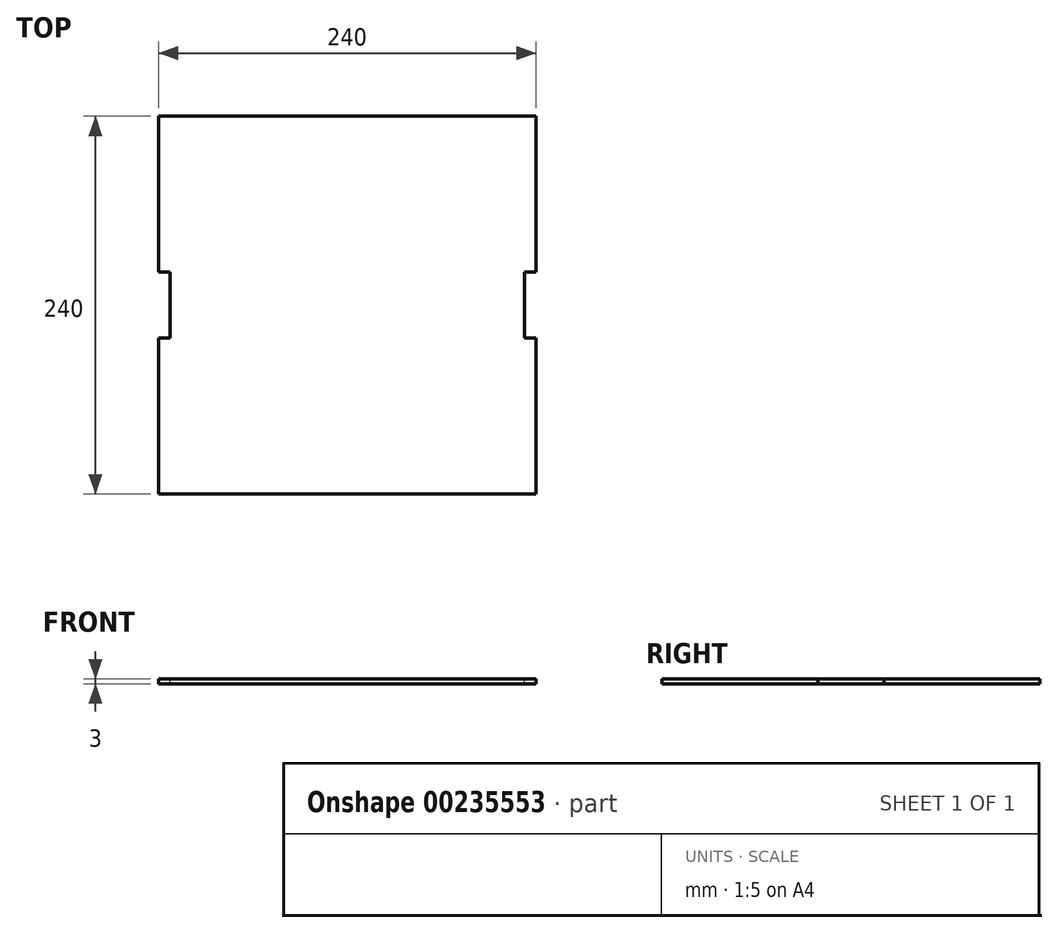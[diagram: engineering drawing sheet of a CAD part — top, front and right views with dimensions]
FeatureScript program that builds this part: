
annotation { "Feature Type Name" : "Feature", "Feature Type Description" : "" }
export const myFeature = defineFeature(function(context is Context, id is Id, definition is map)
    precondition{}
    {
        {
            var Q0;
            Q0=qCreatedBy(makeId("Top.planeOp"),FACE);
            var sketch = newSketch(context, id + "F0", { "sketchPlane" : qUnion([Q0])});
            skLineSegment(sketch, "E0.bottom", {"start": v(120, -120) * mm, "end": v(-120, -120) * mm});
            skLineSegment(sketch, "E0.top", {"start": v(120, 120) * mm, "end": v(-120, 120) * mm});
            skLineSegment(sketch, "E0.left", {"start": v(120, -120) * mm, "end": v(120, 120) * mm});
            skLineSegment(sketch, "E0.right", {"start": v(-120, -120) * mm, "end": v(-120, 120) * mm});
            skPoint(sketch, "E0.middle", {"position": v(0, 0) * mm});
            skSolve(sketch);
        }
        {
            var Q0;
            Q0=makeQuery(id+"F0.imprint","IMPRINT",FACE,{"disambiguationData":[TD([[makeQuery(id+"F0.imprint","IMPRINT",EDGE,{"derivedFrom":sQuery(id+"F0.wireOp",EDGE,"E0.bottom")}),-1.0]])]});
            extrude(context, id + "F1", {"entities" : qUnion([Q0]), "depth" : 3 * mm});
        }
        {
            var Q0;
            Q0=makeQuery(id+"F1.opExtrude","CAP_FACE",FACE,{"disambiguationData":[OSD([sQuery(id+"F0.wireOp",EDGE,"E0.bottom"),sQuery(id+"F0.wireOp",EDGE,"E0.top"),sQuery(id+"F0.wireOp",EDGE,"E0.left"),sQuery(id+"F0.wireOp",EDGE,"E0.right")])],"isStart":false});
            var sketch = newSketch(context, id + "F2", { "sketchPlane" : qUnion([Q0])});
            skLineSegment(sketch, "E1.bottom", {"start": v(-117.5, -21) * mm, "end": v(-122.5, -21) * mm});
            skLineSegment(sketch, "E1.top", {"start": v(-117.5, 21) * mm, "end": v(-122.5, 21) * mm});
            skLineSegment(sketch, "E1.left", {"start": v(-117.5, -21) * mm, "end": v(-117.5, 21) * mm});
            skLineSegment(sketch, "E1.right", {"start": v(-122.5, -21) * mm, "end": v(-122.5, 21) * mm});
            skPoint(sketch, "E1.middle", {"position": v(-120, 0) * mm});
            skLineSegment(sketch, "E2.bottom", {"start": v(122.5, -21) * mm, "end": v(117.5, -21) * mm});
            skLineSegment(sketch, "E2.top", {"start": v(122.5, 21) * mm, "end": v(117.5, 21) * mm});
            skLineSegment(sketch, "E2.left", {"start": v(122.5, -21) * mm, "end": v(122.5, 21) * mm});
            skLineSegment(sketch, "E2.right", {"start": v(117.5, -21) * mm, "end": v(117.5, 21) * mm});
            skPoint(sketch, "E2.middle", {"position": v(120, 0) * mm});
            skLineSegment(sketch, "E3.bottom", {"start": v(-117.5, 21) * mm, "end": v(-112.5, 21) * mm});
            skLineSegment(sketch, "E3.top", {"start": v(-117.5, -21) * mm, "end": v(-112.5, -21) * mm});
            skLineSegment(sketch, "E3.left", {"start": v(-117.5, 21) * mm, "end": v(-117.5, -21) * mm});
            skLineSegment(sketch, "E3.right", {"start": v(-112.5, 21) * mm, "end": v(-112.5, -21) * mm});
            skLineSegment(sketch, "E4.bottom", {"start": v(117.5, 21) * mm, "end": v(112.5, 21) * mm});
            skLineSegment(sketch, "E4.top", {"start": v(117.5, -21) * mm, "end": v(112.5, -21) * mm});
            skLineSegment(sketch, "E4.left", {"start": v(117.5, 21) * mm, "end": v(117.5, -21) * mm});
            skLineSegment(sketch, "E4.right", {"start": v(112.5, 21) * mm, "end": v(112.5, -21) * mm});
            skSolve(sketch);
        }
        {
            var Q0;
            {var subQ0=sQuery(id+"F2.wireOp",EDGE,"E1.left");Q0=makeQuery(id+"F2.imprint","IMPRINT",FACE,{"disambiguationData":[TD([[makeQuery(id+"F2.imprint","IMPRINT",EDGE,{"derivedFrom":subQ0}),1.0]])]});}
            var Q1;
            {var subQ0=sQuery(id+"F2.wireOp",EDGE,"E2.right");Q1=makeQuery(id+"F2.imprint","IMPRINT",FACE,{"disambiguationData":[TD([[makeQuery(id+"F2.imprint","IMPRINT",EDGE,{"derivedFrom":subQ0}),-1.0]])]});}
            var Q2;
            Q2=makeQuery(id+"F2.imprint","IMPRINT",FACE,{"disambiguationData":[TD([[makeQuery(id+"F2.imprint","IMPRINT",EDGE,{"derivedFrom":sQuery(id+"F2.wireOp",EDGE,"E3.bottom")}),-1.0]])]});
            var Q3;
            Q3=makeQuery(id+"F2.imprint","IMPRINT",FACE,{"disambiguationData":[TD([[makeQuery(id+"F2.imprint","IMPRINT",EDGE,{"derivedFrom":sQuery(id+"F2.wireOp",EDGE,"E4.bottom")}),1.0]])]});
            var Q4;
            {var subQ0=sQuery(id+"F2.wireOp",EDGE,"E3.left");Q4=makeQuery(id+"F2.imprint","IMPRINT",FACE,{"disambiguationData":[TD([[makeQuery(id+"F2.imprint","IMPRINT",EDGE,{"derivedFrom":subQ0}),-1.0]])]});}
            var Q5;
            {var subQ0=sQuery(id+"F2.wireOp",EDGE,"E2.left");Q5=makeQuery(id+"F2.imprint","IMPRINT",FACE,{"disambiguationData":[TD([[makeQuery(id+"F2.imprint","IMPRINT",EDGE,{"derivedFrom":subQ0}),1.0]])]});}
            var Q6;
            {var subQ0=sQuery(id+"F2.wireOp",EDGE,"E4.left");Q6=makeQuery(id+"F2.imprint","IMPRINT",FACE,{"disambiguationData":[TD([[makeQuery(id+"F2.imprint","IMPRINT",EDGE,{"derivedFrom":subQ0}),1.0]])]});}
            extrude(context, id + "F3", {"entities" : qUnion([Q0, Q1, Q2, Q3, Q4, Q5, Q6]), "operationType" : NewBodyOperationType.REMOVE, "oppositeDirection" : true, "depth" : 25 * mm});
        }
    });
